# Revit family: VRC-3496
name_source: partatom
category: Lighting Fixtures
units: mm (PartAtom-declared; Revit-internal decimal feet)

## family parameters
Always vertical = Yes
Cut with Voids When Loaded = No
Host = Wall
Light Source = Yes
OmniClass Number = 23.80.70.00
OmniClass Title = Lighting
Part Type = Normal
Room Calculation Point = No
Round Connector Dimension = Use Diameter
Shared = No

## types (5) — shared parameters
Assembly Code = D5020200
Color Filter = 16777215
Description = LED Vandal Resistant Corner Mount
Dimming Lamp Color Temperature Shift = <None>
Emit from Line Length = 2' - 0"
Height = 0' - 7 3/4"
Housing Finish = Metal - Viscor - White
Lamp = LED
Lens Finish = Acrylic - Viscor - Frosted Prismatic P12
Manufacturer = CERTOLUX by VISCOR
Model = VRC-3524
Tilt Angle = -180.00°
URL = https://www.viscor.com
Voltage = 120 V

## per-type parameters (varying)
| type | Apparent Load | Lamp Wattage | Length | Lens Length | Photometric Web File |
| VRC-3496-24-LED840K026Lxxx-P08 | 24 VA | 24 VA | 2' - 0 1/4" | 1' - 10" | VRC-3496-24-LED840K26LUNV-P08.ies |
| VRC-3496-48-LED840K078Lxxx-P08 | 74 VA | 74 VA | 4' - 0 1/4" | 3' - 10" | VRC-3496-48-LED-840K78Lxxx-P08.ies |
| VRC-3496-24-LED840K052Lxxx-P08 | 49 VA | 49 VA | 2' - 0 1/4" | 1' - 10" | VRC-3496-24-LED840K52LUNV-P08.ies |
| VRC-3496-48-LED840K052Lxxx-P13 | 51 VA | 51 VA | 4' - 0 1/4" | 3' - 10" | VRC-3496 48-LED840K52LUNV-P13.ies |
| VRC-3496-48-LED840K026Lxxx-P13 | 24 VA | 24 VA | 4' - 0 1/4" | 3' - 10" | VRC-3496 48-LED840K26LUNV-P13.ies |

## geometry (parser evidence)
native form markers: Sweep x1
no freeform markers — native parametric forms only
